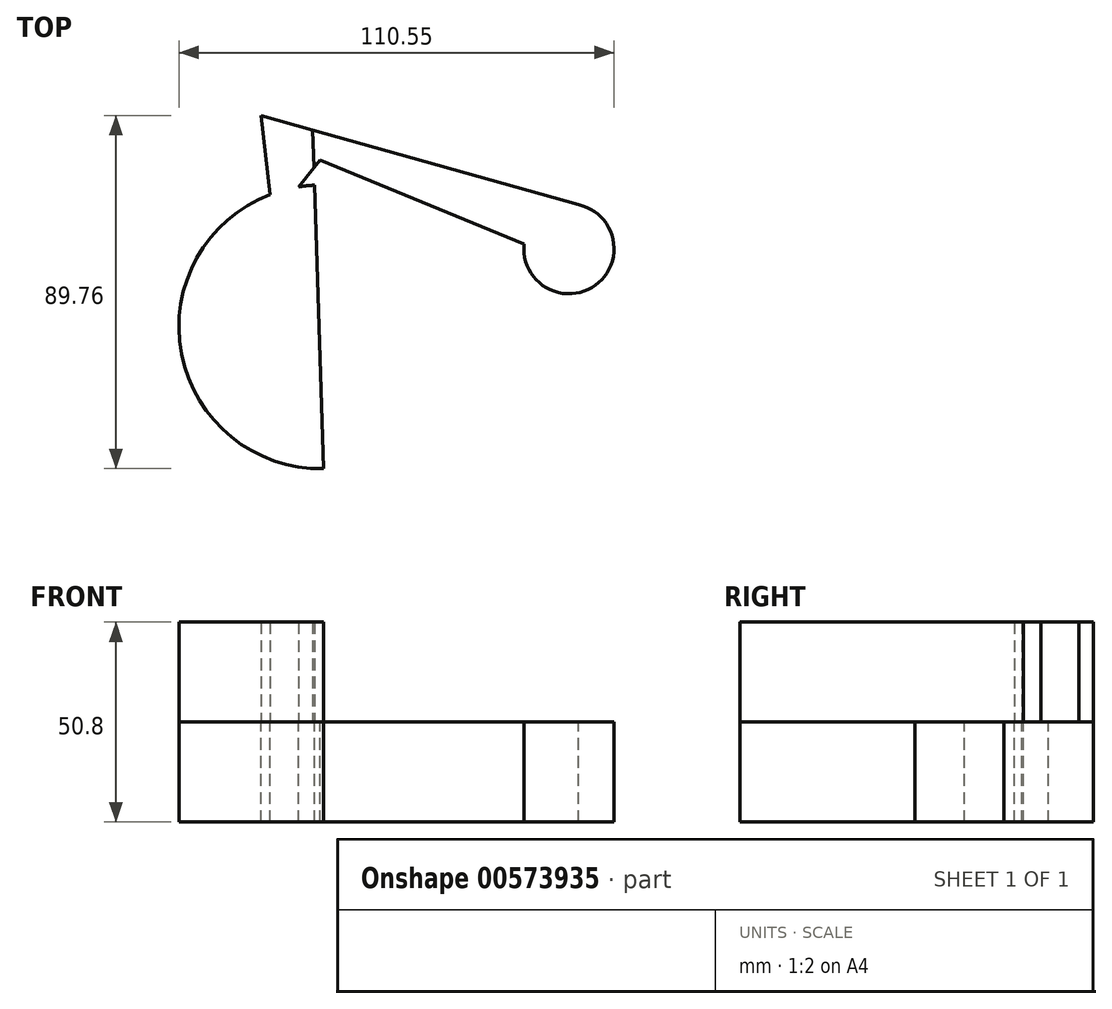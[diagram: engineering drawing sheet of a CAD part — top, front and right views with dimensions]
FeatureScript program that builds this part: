
annotation { "Feature Type Name" : "Feature", "Feature Type Description" : "" }
export const myFeature = defineFeature(function(context is Context, id is Id, definition is map)
    precondition{}
    {
        {
            var Q0;
            Q0=qCreatedBy(makeId("Top.planeOp"),FACE);
            var sketch = newSketch(context, id + "F0", { "sketchPlane" : qUnion([Q0])});
            skArc(sketch, "E0", {"start": v(-49.68, 27.47) * mm, "mid": v(-27.58, -41.01) * mm, "end": v(-42.51, 29.38) * mm});
            skArc(sketch, "E1", {"start": v(14.8, 14.8) * mm, "mid": v(32.92, 4.37) * mm, "end": v(28.66, 24.84) * mm});
            skLineSegment(sketch, "E2", {"start": v(-49.68, 27.47) * mm, "end": v(-52.07, 47.53) * mm});
            skLineSegment(sketch, "E3", {"start": v(-52.07, 47.53) * mm, "end": v(28.66, 24.84) * mm});
            skLineSegment(sketch, "E4", {"start": v(14.8, 14.8) * mm, "end": v(-37.02, 36.18) * mm});
            skPoint(sketch, "E4.endSnap0", {"position": v(-11.7, 36.18) * mm});
            skLineSegment(sketch, "E5", {"start": v(-37.02, 36.18) * mm, "end": v(-42.51, 29.38) * mm});
            skLineSegment(sketch, "E6", {"start": v(-39.89, 76.43) * mm, "end": v(-35.1, -76.67) * mm});
            skSolve(sketch);
        }
        {
            var Q0;
            {var subQ0=sQuery(id+"F0.wireOp",EDGE,"E2");Q0=makeQuery(id+"F0.imprint","IMPRINT",FACE,{"disambiguationData":[TD([[makeQuery(id+"F0.imprint","IMPRINT",EDGE,{"derivedFrom":subQ0}),-1.0]])]});}
            extrude(context, id + "F1", {"entities" : qUnion([Q0]), "depth" : 25.4 * mm, "offsetDistance" : 25.4 * mm});
        }
        {
            var Q0;
            {var subQ0=sQuery(id+"F0.wireOp",EDGE,"E6");var subQ1=sQuery(id+"F0.wireOp",EDGE,"E0");var subQ2=makeQuery(id+"F0.imprint","INTERSECT",VERTEX,{"disambiguationData":[OD(0.0)],"derivedFrom":[subQ1,subQ0]});Q0=makeQuery(id+"F0.imprint","IMPRINT",FACE,{"disambiguationData":[TD([[makeQuery(id+"F0.imprint","IMPRINT",EDGE,{"disambiguationData":[TD([[subQ2,-1.0]])],"derivedFrom":subQ1}),1.0]])]});}
            var Q1;
            {var subQ2=sQuery(id+"F0.wireOp",EDGE,"E1");Q1=makeQuery(id+"F0.imprint","IMPRINT",FACE,{"disambiguationData":[TD([[makeQuery(id+"F0.imprint","IMPRINT",EDGE,{"derivedFrom":subQ2}),1.0]])]});}
            extrude(context, id + "F2", {"entities" : qUnion([Q0, Q1]), "depth" : -25.4 * mm, "offsetDistance" : 25.4 * mm});
        }
    });
